# Revit family: 447_d-DN125-RFA_2019
name_source: partatom
category: Pipe Accessories
units: mm (PartAtom-declared; Revit-internal decimal feet)

## family parameters
Always vertical = Yes
Cut with Voids When Loaded = No
Part Type = Valve - Breaks Into
Round Connector Dimension = Use Diameter
Shared = No
Work Plane-Based = No

## types (10) — shared parameters
Description = Ruční vyvažovací ventil s drážkovým spojem
L2D = 350 mm
L2D_Min = 3048 mm
Manufacturer = Hydronix
QmdConnectorList = 301;D;302;D
Type Comments = drážkový spoj; PN16; -10~+120°C;
URL = www.hydronix.cz
W2D = 100 mm
magiPartTypeId = 304
magiProductFamilyId = eab8c084d85f47fc9aed3208e9defb

## per-type parameters (varying)
- 447_d-DN100: CenSd_R13_6=7 mm; D=100 mm; H10=22 mm; H11=26 mm; H13=24 mm; H14=32 mm; H15=87 mm; H16=5 mm  [stored 0.0164042 ft]; H17=10 mm  [stored 0.0328084 ft]; H4=48 mm; H5=13 mm; H6=19 mm; H7=16 mm; H8=42 mm; H9=6 mm; KL=51 mm; KZ=29 mm; L1=175 mm; L10=30 mm; L11=14 mm  [stored 0.0459318 ft]; L12=13 mm; L13=13 mm; L2=17 mm; L2__ve=-17 mm; L3=10 mm  [stored 0.0328084 ft]; L3__ve=-10 mm  [stored -0.0328084 ft]; L4=7 mm; L4__ve=-7 mm; L5=5 mm  [stored 0.0164042 ft]; L6=78 mm; L8=26 mm; L8__ve=-26 mm; L9=52 mm; MC Product Code=447 100 d (DN100; PN16 kvs180,5); R=50 mm; R1=57 mm; R11=7 mm; R12=6 mm; R13=8 mm  [stored 0.0262467 ft]; R2=54 mm; R3=63 mm; R4=31 mm; R5=65 mm; R6=68 mm; R7=34 mm; R8=31 mm; R9=74 mm; W1=13 mm; W2=30 mm; W3=14 mm  [stored 0.0459318 ft]; magiProductId=e5a6bfdd9ca54003a0551f5d760c3c
- 447_d-DN125: CenSd_R13_6=7 mm; D=125 mm; H10=25 mm; H11=28 mm; H13=26 mm; H14=35 mm; H15=104 mm; H16=5 mm  [stored 0.0164042 ft]; H17=10 mm  [stored 0.0328084 ft]; H4=53 mm; H5=14 mm  [stored 0.0459318 ft]; H6=21 mm; H7=18 mm; H8=46 mm; H9=7 mm; KL=58 mm; KZ=33 mm; L1=200 mm; L10=30 mm; L11=14 mm  [stored 0.0459318 ft]; L12=13 mm; L13=15 mm  [stored 0.0492126 ft]; L2=19 mm; L2__ve=-19 mm; L3=11 mm; L3__ve=-11 mm; L4=8 mm  [stored 0.0262467 ft]; L4__ve=-8 mm; L5=6 mm; L6=90 mm; L8=30 mm; L8__ve=-30 mm; L9=60 mm; MC Product Code=447 125 d (DN125; PN16 kvs280,0); R=63 mm; R1=71 mm; R11=7 mm; R12=7 mm; R13=9 mm; R2=67 mm; R3=78 mm; R4=39 mm; R5=65 mm; R6=85 mm; R7=42 mm; R8=39 mm; R9=92 mm; W1=13 mm; W2=30 mm; W3=14 mm  [stored 0.0459318 ft]; magiProductId=5795ec580370482d8c46e49d975863
- 447_d-DN150: CenSd_R13_6=9 mm; D=150 mm; H10=27 mm; H11=31 mm; H13=29 mm; H14=39 mm; H15=121 mm; H16=6 mm; H17=11 mm; H4=58 mm; H5=16 mm; H6=23 mm; H7=19 mm; H8=51 mm; H9=8 mm  [stored 0.0262467 ft]; KL=69 mm; KZ=40 mm; L1=240 mm; L10=30 mm; L11=14 mm  [stored 0.0459318 ft]; L12=13 mm; L13=18 mm; L2=23 mm; L2__ve=-23 mm; L3=14 mm  [stored 0.0459318 ft]; L3__ve=-14 mm; L4=9 mm; L4__ve=-9 mm; L5=7 mm; L6=107 mm; L8=36 mm; L8__ve=-36 mm; L9=72 mm; MC Product Code=447 150 d (DN150; PN16 kvs383,4); R=75 mm; R1=84 mm; R11=9 mm; R12=8 mm  [stored 0.0262467 ft]; R13=10 mm  [stored 0.0328084 ft]; R2=80 mm; R3=92 mm; R4=46 mm; R5=65 mm; R6=101 mm; R7=50 mm; R8=46 mm; R9=109 mm; W1=13 mm; W2=30 mm; W3=14 mm  [stored 0.0459318 ft]; magiProductId=9b6b5ad10a674c51b522359e7e2d39
- 447_d-DN200: CenSd_R13_6=11 mm; D=200 mm; H10=43 mm; H11=50 mm; H13=46 mm; H14=62 mm; H15=168 mm; H16=10 mm  [stored 0.0328084 ft]; H17=19 mm; H4=93 mm; H5=25 mm; H6=37 mm; H7=31 mm; H8=81 mm; H9=12 mm  [stored 0.0393701 ft]; KL=87 mm; KZ=50 mm; L1=300 mm; L10=72 mm; L11=32 mm; L12=30 mm; L13=22 mm; L2=29 mm; L2__ve=-29 mm; L3=17 mm; L3__ve=-17 mm; L4=11 mm; L4__ve=-11 mm; L5=9 mm; L6=134 mm; L8=45 mm; L8__ve=-45 mm; L9=90 mm; MC Product Code=447 200 d (DN200; PN16 kvs710,0); R=100 mm; R1=110 mm; R11=11 mm; R12=10 mm  [stored 0.0328084 ft]; R13=13 mm; R2=104 mm; R3=120 mm; R4=60 mm; R5=155 mm; R6=131 mm; R7=66 mm; R8=60 mm; R9=142 mm; W1=30 mm; W2=72 mm; W3=32 mm; magiProductId=f5a67fe5c2444fc986ed7f87b9a4ed
- 447_d-DN250: CenSd_R13_6=14 mm  [stored 0.0459318 ft]; D=250 mm; H10=48 mm; H11=55 mm; H13=52 mm; H14=69 mm; H15=203 mm; H16=11 mm; H17=21 mm; H4=103 mm; H5=28 mm; H6=41 mm; H7=34 mm; H8=90 mm; H9=14 mm  [stored 0.0459318 ft]; KL=105 mm; KZ=61 mm; L1=365 mm; L10=72 mm; L11=32 mm; L12=30 mm; L13=27 mm; L2=35 mm; L2__ve=-35 mm; L3=21 mm; L3__ve=-21 mm; L4=14 mm  [stored 0.0459318 ft]; L4__ve=-14 mm; L5=10 mm  [stored 0.0328084 ft]; L6=163 mm; L8=54 mm; L8__ve=-54 mm; L9=109 mm; MC Product Code=447 250 d (DN250; PN16 kvs1187,5); R=125 mm; R1=137 mm; R11=14 mm  [stored 0.0459318 ft]; R12=12 mm  [stored 0.0393701 ft]; R13=16 mm; R2=130 mm; R3=150 mm; R4=75 mm; R5=155 mm; R6=164 mm; R7=82 mm; R8=75 mm; R9=177 mm; W1=30 mm; W2=72 mm; W3=32 mm; magiProductId=7d63ae0d28f64990bc8ce3477101ef
- 447_d-DN300: CenSd_R13_6=16 mm; D=300 mm; H10=49 mm; H11=56 mm; H13=53 mm; H14=70 mm; H15=232 mm; H16=11 mm; H17=21 mm; H4=106 mm; H5=28 mm; H6=42 mm; H7=35 mm; H8=92 mm; H9=14 mm  [stored 0.0459318 ft]; KL=123 mm; KZ=71 mm; L1=425 mm; L10=72 mm; L11=32 mm; L12=30 mm; L13=32 mm; L2=40 mm; L2__ve=-40 mm; L3=24 mm; L3__ve=-24 mm; L4=16 mm; L4__ve=-16 mm; L5=12 mm  [stored 0.0393701 ft]; L6=190 mm; L8=63 mm; L8__ve=-63 mm; L9=127 mm; MC Product Code=447 300 d (DN300; PN16 kvs1504,1); R=150 mm; R1=162 mm; R11=16 mm; R12=14 mm  [stored 0.0459318 ft]; R13=18 mm; R2=154 mm; R3=178 mm; R4=89 mm; R5=155 mm; R6=194 mm; R7=97 mm; R8=89 mm; R9=211 mm; W1=30 mm; W2=72 mm; W3=32 mm; magiProductId=0a2a34dba99a430aa7daf784d6b0c1
- 447_d-DN040: CenSd_R13_6=4 mm  [stored 0.0131234 ft]; D=40 mm; H10=12 mm  [stored 0.0393701 ft]; H11=14 mm  [stored 0.0459318 ft]; H13=13 mm; H14=17 mm; H15=39 mm; H16=3 mm  [stored 0.00984252 ft]; H17=5 mm  [stored 0.0164042 ft]; H4=26 mm; H5=7 mm; H6=10 mm  [stored 0.0328084 ft]; H7=9 mm; H8=22 mm; H9=3 mm  [stored 0.00984252 ft]; KL=29 mm; KZ=17 mm; L1=100 mm; L10=17 mm; L11=9 mm; L12=7 mm; L13=7 mm; L2=10 mm  [stored 0.0328084 ft]; L2__ve=-10 mm  [stored -0.0328084 ft]; L3=6 mm; L3__ve=-6 mm; L4=4 mm  [stored 0.0131234 ft]; L4__ve=-4 mm; L5=3 mm  [stored 0.00984252 ft]; L6=45 mm; L8=15 mm  [stored 0.0492126 ft]; L8__ve=-15 mm; L9=30 mm; MC Product Code=447 040 d (DN40; PN16 kvs22,36); R=20 mm; R1=24 mm; R11=4 mm  [stored 0.0131234 ft]; R12=3 mm  [stored 0.00984252 ft]; R13=4 mm  [stored 0.0131234 ft]; R2=23 mm; R3=26 mm; R4=13 mm; R5=37 mm; R6=29 mm; R7=14 mm  [stored 0.0459318 ft]; R8=13 mm; R9=31 mm; W1=7 mm; W2=17 mm; W3=9 mm; magiProductId=6dc4a6b5eb924103b02307904d600f
- 447_d-DN050: CenSd_R13_6=4 mm  [stored 0.0131234 ft]; D=50 mm; H10=12 mm  [stored 0.0393701 ft]; H11=14 mm  [stored 0.0459318 ft]; H13=13 mm; H14=17 mm; H15=46 mm; H16=3 mm  [stored 0.00984252 ft]; H17=5 mm  [stored 0.0164042 ft]; H4=26 mm; H5=7 mm; H6=10 mm  [stored 0.0328084 ft]; H7=9 mm; H8=22 mm; H9=3 mm  [stored 0.00984252 ft]; KL=33 mm; KZ=19 mm; L1=115 mm; L10=17 mm; L11=9 mm; L12=7 mm; L13=9 mm; L2=11 mm; L2__ve=-11 mm; L3=7 mm; L3__ve=-7 mm; L4=4 mm  [stored 0.0131234 ft]; L4__ve=-4 mm; L5=3 mm  [stored 0.00984252 ft]; L6=51 mm; L8=17 mm; L8__ve=-17 mm; L9=34 mm; MC Product Code=447 050 d (DN50; PN16 kvs32,15); R=25 mm; R1=30 mm; R11=4 mm  [stored 0.0131234 ft]; R12=4 mm  [stored 0.0131234 ft]; R13=5 mm  [stored 0.0164042 ft]; R2=29 mm; R3=33 mm; R4=17 mm; R5=37 mm; R6=36 mm; R7=18 mm; R8=17 mm; R9=39 mm; W1=7 mm; W2=17 mm; W3=9 mm; magiProductId=b59a3d0ad4654cda90cee0c397c848
- 447_d-DN065: CenSd_R13_6=5 mm  [stored 0.0164042 ft]; D=65 mm; H10=20 mm; H11=23 mm; H13=22 mm; H14=29 mm; H15=64 mm; H16=4 mm  [stored 0.0131234 ft]; H17=9 mm; H4=43 mm; H5=12 mm  [stored 0.0393701 ft]; H6=17 mm; H7=14 mm  [stored 0.0459318 ft]; H8=38 mm; H9=6 mm; KL=42 mm; KZ=24 mm; L1=145 mm; L10=30 mm; L11=14 mm  [stored 0.0459318 ft]; L12=13 mm; L13=11 mm; L2=14 mm  [stored 0.0459318 ft]; L2__ve=-14 mm; L3=8 mm  [stored 0.0262467 ft]; L3__ve=-8 mm; L4=6 mm; L4__ve=-6 mm; L5=4 mm  [stored 0.0131234 ft]; L6=65 mm; L8=22 mm; L8__ve=-22 mm; L9=43 mm; MC Product Code=447 065 d (DN65; PN16 kvs83,3); R=33 mm; R1=38 mm; R11=5 mm  [stored 0.0164042 ft]; R12=5 mm  [stored 0.0164042 ft]; R13=6 mm; R2=36 mm; R3=42 mm; R4=21 mm; R5=65 mm; R6=46 mm; R7=23 mm; R8=21 mm; R9=49 mm; W1=13 mm; W2=30 mm; W3=14 mm  [stored 0.0459318 ft]; magiProductId=356db372cd37496c9ff0d3ad255dc6
- 447_d-DN080: CenSd_R13_6=6 mm; D=80 mm; H10=20 mm; H11=23 mm; H13=22 mm; H14=29 mm; H15=71 mm; H16=4 mm  [stored 0.0131234 ft]; H17=9 mm; H4=43 mm; H5=12 mm  [stored 0.0393701 ft]; H6=17 mm; H7=14 mm  [stored 0.0459318 ft]; H8=38 mm; H9=6 mm; KL=45 mm; KZ=26 mm; L1=155 mm; L10=30 mm; L11=14 mm  [stored 0.0459318 ft]; L12=13 mm; L13=12 mm  [stored 0.0393701 ft]; L2=15 mm  [stored 0.0492126 ft]; L2__ve=-15 mm; L3=9 mm; L3__ve=-9 mm; L4=6 mm; L4__ve=-6 mm; L5=4 mm  [stored 0.0131234 ft]; L6=69 mm; L8=23 mm; L8__ve=-23 mm; L9=46 mm; MC Product Code=447 080 d (DN80; PN16 kvs104,3); R=40 mm; R1=45 mm; R11=6 mm; R12=5 mm  [stored 0.0164042 ft]; R13=7 mm; R2=42 mm; R3=49 mm; R4=24 mm; R5=65 mm; R6=53 mm; R7=27 mm; R8=24 mm; R9=58 mm; W1=13 mm; W2=30 mm; W3=14 mm  [stored 0.0459318 ft]; magiProductId=f43aa02b4841429783243073d22ea7

note: [stored X ft] marks values corroborated as IEEE doubles in the binary element streams (Revit-internal decimal feet)

## geometry (parser evidence)
native form markers: Sweep x1
no freeform markers — native parametric forms only
